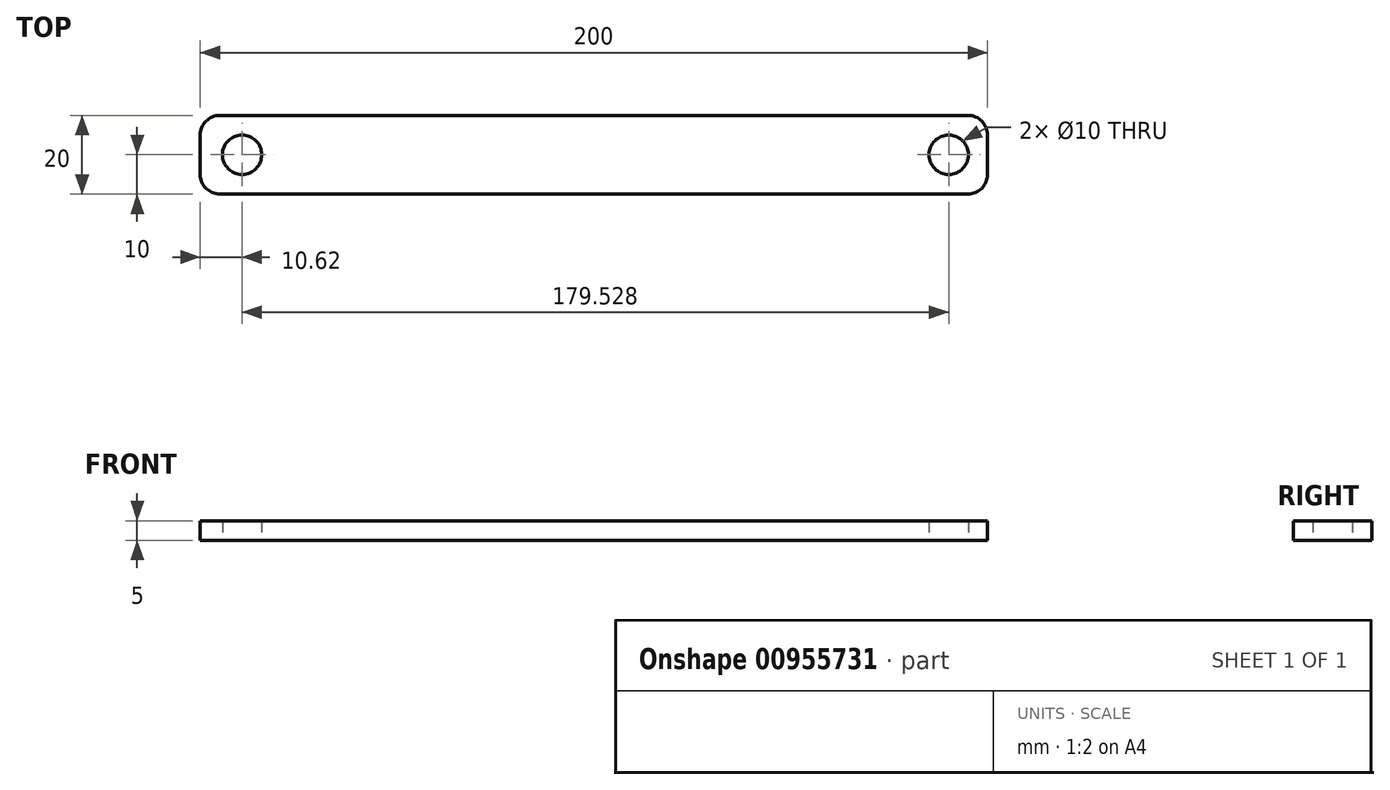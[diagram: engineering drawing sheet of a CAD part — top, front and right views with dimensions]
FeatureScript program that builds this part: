
annotation { "Feature Type Name" : "Feature", "Feature Type Description" : "" }
export const myFeature = defineFeature(function(context is Context, id is Id, definition is map)
    precondition{}
    {
        {
            var Q0;
            Q0=qCreatedBy(makeId("Top.planeOp"),FACE);
            var sketch = newSketch(context, id + "F0", { "sketchPlane" : qUnion([Q0])});
            skLineSegment(sketch, "E0.bottom", {"start": v(100, 10) * mm, "end": v(-100, 10) * mm});
            skLineSegment(sketch, "E0.top", {"start": v(100, -10) * mm, "end": v(-100, -10) * mm});
            skLineSegment(sketch, "E0.left", {"start": v(100, 10) * mm, "end": v(100, -10) * mm});
            skLineSegment(sketch, "E0.right", {"start": v(-100, 10) * mm, "end": v(-100, -10) * mm});
            skPoint(sketch, "E0.middle", {"position": v(0, 0) * mm});
            skCircle(sketch, "E1", {"center": v(-89.38, 0) * mm, "radius": 5 * mm});
            skCircle(sketch, "E2", {"center": v(90.15, 0) * mm, "radius": 5 * mm});
            skSolve(sketch);
        }
        {
            var Q0;
            Q0=makeQuery(id+"F0.imprint","IMPRINT",FACE,{"disambiguationData":[TD([[makeQuery(id+"F0.imprint","IMPRINT",EDGE,{"derivedFrom":sQuery(id+"F0.wireOp",EDGE,"E0.bottom")}),1.0]])]});
            extrude(context, id + "F1", {"entities" : qUnion([Q0]), "depth" : 5 * mm, "offsetDistance" : 25 * mm});
        }
        {
            var Q0;
            Q0=makeQuery(id+"F1.opExtrude","SWEPT_EDGE",EDGE,{"disambiguationData":[OSD([sQuery(id+"F0.wireOp",EDGE,"E0.top"),sQuery(id+"F0.wireOp",EDGE,"E0.right")])]});
            var Q1;
            Q1=makeQuery(id+"F1.opExtrude","SWEPT_EDGE",EDGE,{"disambiguationData":[OSD([sQuery(id+"F0.wireOp",EDGE,"E0.top"),sQuery(id+"F0.wireOp",EDGE,"E0.left")])]});
            var Q2;
            Q2=makeQuery(id+"F1.opExtrude","SWEPT_EDGE",EDGE,{"disambiguationData":[OSD([sQuery(id+"F0.wireOp",EDGE,"E0.bottom"),sQuery(id+"F0.wireOp",EDGE,"E0.left")])]});
            var Q3;
            Q3=makeQuery(id+"F1.opExtrude","SWEPT_EDGE",EDGE,{"disambiguationData":[OSD([sQuery(id+"F0.wireOp",EDGE,"E0.bottom"),sQuery(id+"F0.wireOp",EDGE,"E0.right")])]});
            fillet(context, id + "F2", {"entities" : qUnion([Q0, Q1, Q2, Q3]), "radius" : 5 * mm, "tangentPropagation" : true, "allowEdgeOverflow" : false});
        }
    });
